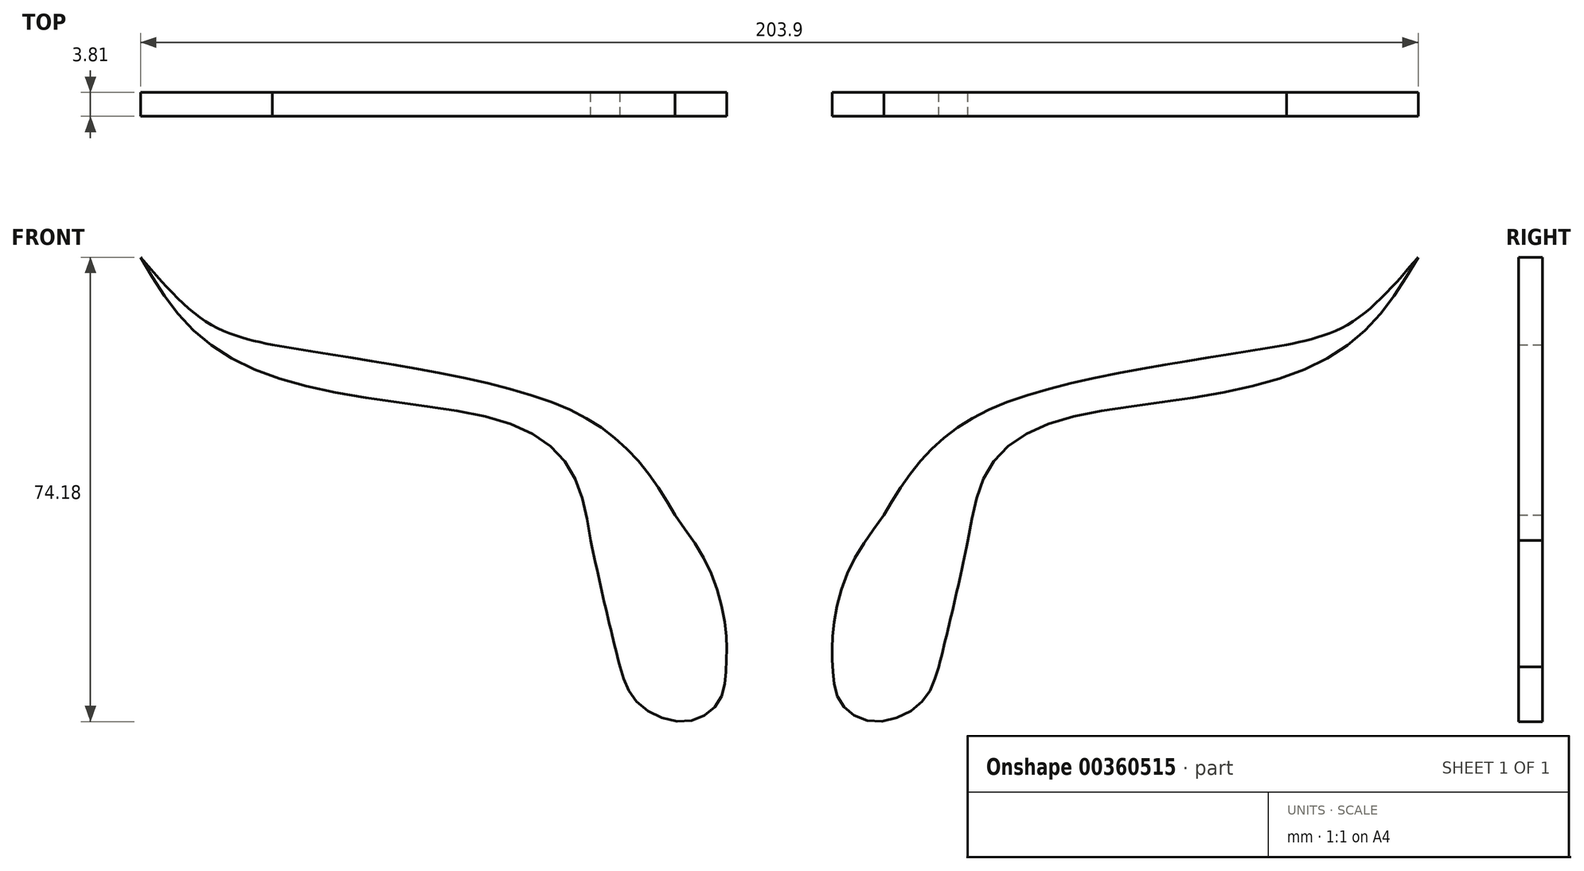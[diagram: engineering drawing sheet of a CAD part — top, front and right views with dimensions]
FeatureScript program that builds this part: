
annotation { "Feature Type Name" : "Feature", "Feature Type Description" : "" }
export const myFeature = defineFeature(function(context is Context, id is Id, definition is map)
    precondition{}
    {
        {
            var Q0;
            Q0=qCreatedBy(makeId("Front.planeOp"),FACE);
            var sketch = newSketch(context, id + "F0", { "sketchPlane" : qUnion([Q0])});
            skPoint(sketch, "E0", {"position": v(-101.95, 50.52) * mm});
            skPoint(sketch, "E1", {"position": v(-94.65, 40) * mm});
            skPoint(sketch, "E2", {"position": v(-82.67, 32.12) * mm});
            skPoint(sketch, "E3", {"position": v(-61.65, 27.45) * mm});
            skPoint(sketch, "E4", {"position": v(-41.5, 23.36) * mm});
            skPoint(sketch, "E5", {"position": v(-33.03, 16.06) * mm});
            skPoint(sketch, "E6", {"position": v(-30.11, 5.26) * mm});
            skPoint(sketch, "E7", {"position": v(-27.78, -5.26) * mm});
            skPoint(sketch, "E8", {"position": v(-25.44, -14.9) * mm});
            skPoint(sketch, "E9", {"position": v(-15.22, -23.65) * mm});
            skPoint(sketch, "E10", {"position": v(-8.5, -14.9) * mm});
            skPoint(sketch, "E11", {"position": v(-8.5, -9.64) * mm});
            skPoint(sketch, "E12", {"position": v(-10.84, 0) * mm});
            skPoint(sketch, "E13", {"position": v(-16.68, 9.34) * mm});
            skPoint(sketch, "E14", {"position": v(-23.98, 19.56) * mm});
            skPoint(sketch, "E15", {"position": v(-36.54, 27.45) * mm});
            skPoint(sketch, "E16", {"position": v(-61.36, 33.29) * mm});
            skPoint(sketch, "E17", {"position": v(-80.92, 36.5) * mm});
            skFitSpline(sketch, "E18", {"points": [v(-101.95, 50.52) * mm, v(-94.65, 40) * mm, v(-82.67, 32.12) * mm, v(-61.65, 27.45) * mm, v(-41.5, 23.36) * mm, v(-33.03, 16.06) * mm, v(-30.11, 5.26) * mm], "startDerivative": vector(42.5, -72) * mm, "endDerivative": vector(12.6, -79.7) * mm});
            skFitSpline(sketch, "E19", {"points": [v(-30.11, 5.26) * mm, v(-27.78, -5.26) * mm, v(-25.44, -14.9) * mm], "startDerivative": vector(4.53, -20.83) * mm, "endDerivative": vector(4.82, -19.45) * mm});
            skPoint(sketch, "E20", {"position": v(-22.81, -20.44) * mm});
            skPoint(sketch, "E21", {"position": v(-9.67, -20.44) * mm});
            skFitSpline(sketch, "E22", {"points": [v(-25.44, -14.9) * mm, v(-22.81, -20.44) * mm, v(-15.22, -23.65) * mm, v(-9.67, -20.44) * mm, v(-8.5, -14.9) * mm, v(-8.5, -9.64) * mm, v(-10.84, 0) * mm, v(-16.68, 9.34) * mm], "startDerivative": vector(13.42, -44.72) * mm, "endDerivative": vector(-37.7, 52.63) * mm});
            skFitSpline(sketch, "E23", {"points": [v(-16.68, 9.34) * mm, v(-23.98, 19.56) * mm, v(-36.54, 27.45) * mm, v(-61.36, 33.29) * mm, v(-80.92, 36.5) * mm], "startDerivative": vector(-27.63, 49.97) * mm, "endDerivative": vector(-69.74, 11.1) * mm});
            skPoint(sketch, "E24", {"position": v(-91.14, 40) * mm});
            skFitSpline(sketch, "E25", {"points": [v(-80.92, 36.5) * mm, v(-91.14, 40) * mm, v(-101.95, 50.52) * mm], "startDerivative": vector(-22.83, 4.95) * mm, "endDerivative": vector(-19.32, 22.6) * mm});
            skPoint(sketch, "E26.MirrorP", {"position": v(94.65, 40) * mm});
            skPoint(sketch, "E27.MirrorP", {"position": v(8.5, -14.9) * mm});
            skPoint(sketch, "E28.MirrorP", {"position": v(30.11, 5.26) * mm});
            skPoint(sketch, "E29.MirrorP", {"position": v(9.67, -20.44) * mm});
            skPoint(sketch, "E30.MirrorP", {"position": v(80.92, 36.5) * mm});
            skPoint(sketch, "E31.MirrorP", {"position": v(16.68, 9.34) * mm});
            skPoint(sketch, "E32.MirrorP", {"position": v(8.5, -9.64) * mm});
            skPoint(sketch, "E33.MirrorP", {"position": v(91.14, 40) * mm});
            skPoint(sketch, "E34.MirrorP", {"position": v(27.78, -5.26) * mm});
            skPoint(sketch, "E35.MirrorP", {"position": v(61.65, 27.45) * mm});
            skPoint(sketch, "E36.MirrorP", {"position": v(41.5, 23.36) * mm});
            skPoint(sketch, "E37.MirrorP", {"position": v(33.03, 16.06) * mm});
            skFitSpline(sketch, "E38.MirrorCS", {"points": [v(101.95, 50.52) * mm, v(94.65, 40) * mm, v(82.67, 32.12) * mm, v(61.65, 27.45) * mm, v(41.5, 23.36) * mm, v(33.03, 16.06) * mm, v(30.11, 5.26) * mm], "startDerivative": vector(-42.5, -72) * mm, "endDerivative": vector(-12.6, -79.7) * mm});
            skFitSpline(sketch, "E39.MirrorCS", {"points": [v(30.11, 5.26) * mm, v(27.78, -5.26) * mm, v(25.44, -14.9) * mm], "startDerivative": vector(-4.53, -20.83) * mm, "endDerivative": vector(-4.82, -19.45) * mm});
            skFitSpline(sketch, "E40.MirrorCS", {"points": [v(25.44, -14.9) * mm, v(22.81, -20.44) * mm, v(15.22, -23.65) * mm, v(9.67, -20.44) * mm, v(8.5, -14.9) * mm, v(8.5, -9.64) * mm, v(10.84, 0) * mm, v(16.68, 9.34) * mm], "startDerivative": vector(-13.42, -44.72) * mm, "endDerivative": vector(37.7, 52.63) * mm});
            skFitSpline(sketch, "E41.MirrorCS", {"points": [v(16.68, 9.34) * mm, v(23.98, 19.56) * mm, v(36.54, 27.45) * mm, v(61.36, 33.29) * mm, v(80.92, 36.5) * mm], "startDerivative": vector(27.63, 49.97) * mm, "endDerivative": vector(69.74, 11.1) * mm});
            skFitSpline(sketch, "E42.MirrorCS", {"points": [v(80.92, 36.5) * mm, v(91.14, 40) * mm, v(101.95, 50.52) * mm], "startDerivative": vector(22.83, 4.95) * mm, "endDerivative": vector(19.32, 22.6) * mm});
            skSolve(sketch);
        }
        {
            var Q0;
            Q0 = qSketchRegion(id + "F0", true);
            extrude(context, id + "F1", {"entities" : qUnion([Q0]), "depth" : 3.8 * mm});
        }
    });
